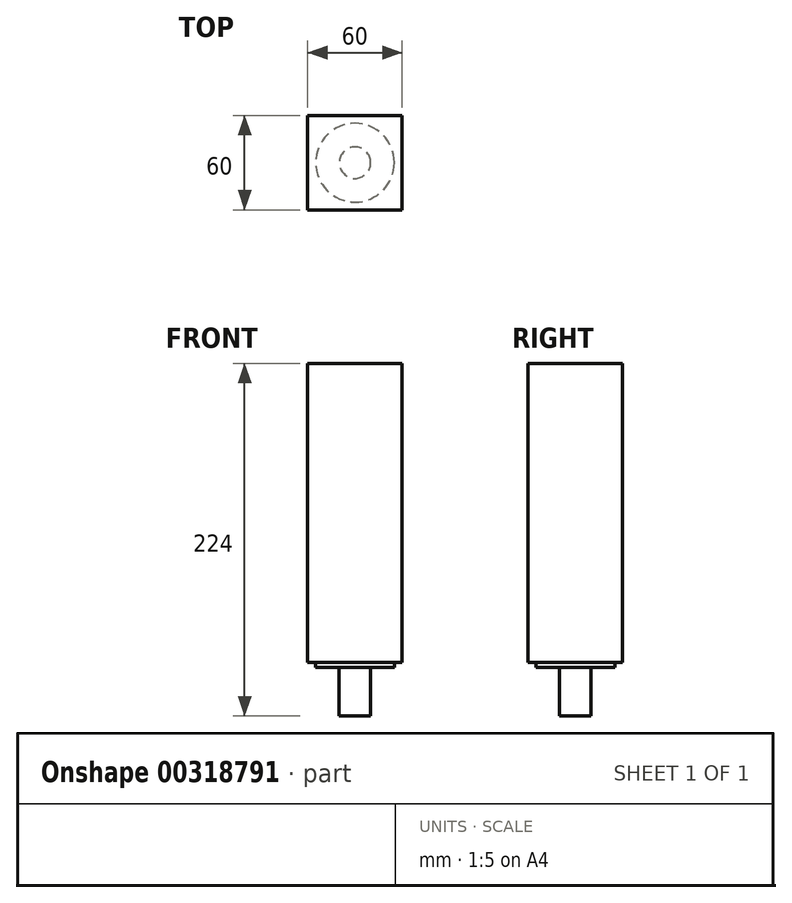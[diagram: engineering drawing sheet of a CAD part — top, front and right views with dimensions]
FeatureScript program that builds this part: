
annotation { "Feature Type Name" : "Feature", "Feature Type Description" : "" }
export const myFeature = defineFeature(function(context is Context, id is Id, definition is map)
    precondition{}
    {
        {
            var Q0;
            Q0=qCreatedBy(makeId("Top.planeOp"),FACE);
            var sketch = newSketch(context, id + "F0", { "sketchPlane" : qUnion([Q0])});
            skCircle(sketch, "E0", {"center": v(0, 0) * mm, "radius": 10 * mm});
            skSolve(sketch);
        }
        {
            var Q0;
            Q0=makeQuery(id+"F0.imprint","IMPRINT",FACE,{"disambiguationData":[TD([[makeQuery(id+"F0.imprint","IMPRINT",EDGE,{"derivedFrom":sQuery(id+"F0.wireOp",EDGE,"E0")}),1.0]])]});
            extrude(context, id + "F1", {"entities" : qUnion([Q0]), "depth" : 31 * mm});
        }
        {
            var Q0;
            Q0=makeQuery(id+"F1.opExtrude","CAP_FACE",FACE,{"disambiguationData":[OSD([sQuery(id+"F0.wireOp",EDGE,"E0")])],"isStart":false});
            var sketch = newSketch(context, id + "F2", { "sketchPlane" : qUnion([Q0])});
            skCircle(sketch, "E1", {"center": v(0, 0) * mm, "radius": 25 * mm});
            skSolve(sketch);
        }
        {
            var Q0;
            Q0=makeQuery(id+"F2.imprint","IMPRINT",FACE,{"disambiguationData":[TD([[makeQuery(id+"F2.imprint","IMPRINT",EDGE,{"derivedFrom":sQuery(id+"F2.wireOp",EDGE,"E1")}),1.0]])]});
            var Q1;
            Q1=makeQuery(id+"F2.imprint","IMPRINT",FACE,{"disambiguationData":[TD([[makeQuery(id+"F2.imprint","IMPRINT",EDGE,{"derivedFrom":makeQuery(id+"F1.opExtrude","CAP_EDGE",EDGE,{"disambiguationData":[OSD([sQuery(id+"F0.wireOp",EDGE,"E0")])],"isStart":false})}),1.0]])]});
            extrude(context, id + "F3", {"entities" : qUnion([Q0, Q1]), "operationType" : NewBodyOperationType.ADD, "depth" : 3 * mm});
        }
        {
            var Q0;
            Q0=makeQuery(id+"F3.opExtrude","CAP_FACE",FACE,{"disambiguationData":[OSD([sQuery(id+"F2.wireOp",EDGE,"E1")])],"isStart":false});
            var sketch = newSketch(context, id + "F4", { "sketchPlane" : qUnion([Q0])});
            skLineSegment(sketch, "E2.bottom", {"start": v(30, 30) * mm, "end": v(-30, 30) * mm});
            skLineSegment(sketch, "E2.top", {"start": v(30, -30) * mm, "end": v(-30, -30) * mm});
            skLineSegment(sketch, "E2.left", {"start": v(30, 30) * mm, "end": v(30, -30) * mm});
            skLineSegment(sketch, "E2.right", {"start": v(-30, 30) * mm, "end": v(-30, -30) * mm});
            skPoint(sketch, "E2.middle", {"position": v(0, 0) * mm});
            skSolve(sketch);
        }
        {
            var Q0;
            Q0=makeQuery(id+"F4.imprint","IMPRINT",FACE,{"disambiguationData":[TD([[makeQuery(id+"F4.imprint","IMPRINT",EDGE,{"derivedFrom":sQuery(id+"F4.wireOp",EDGE,"E2.bottom")}),1.0]])]});
            var Q1;
            Q1=makeQuery(id+"F4.imprint","IMPRINT",FACE,{"disambiguationData":[TD([[makeQuery(id+"F4.imprint","IMPRINT",EDGE,{"derivedFrom":makeQuery(id+"F3.opExtrude","CAP_EDGE",EDGE,{"disambiguationData":[OSD([sQuery(id+"F2.wireOp",EDGE,"E1")])],"isStart":false})}),1.0]])]});
            extrude(context, id + "F5", {"entities" : qUnion([Q0, Q1]), "operationType" : NewBodyOperationType.ADD, "depth" : 190 * mm});
        }
    });
